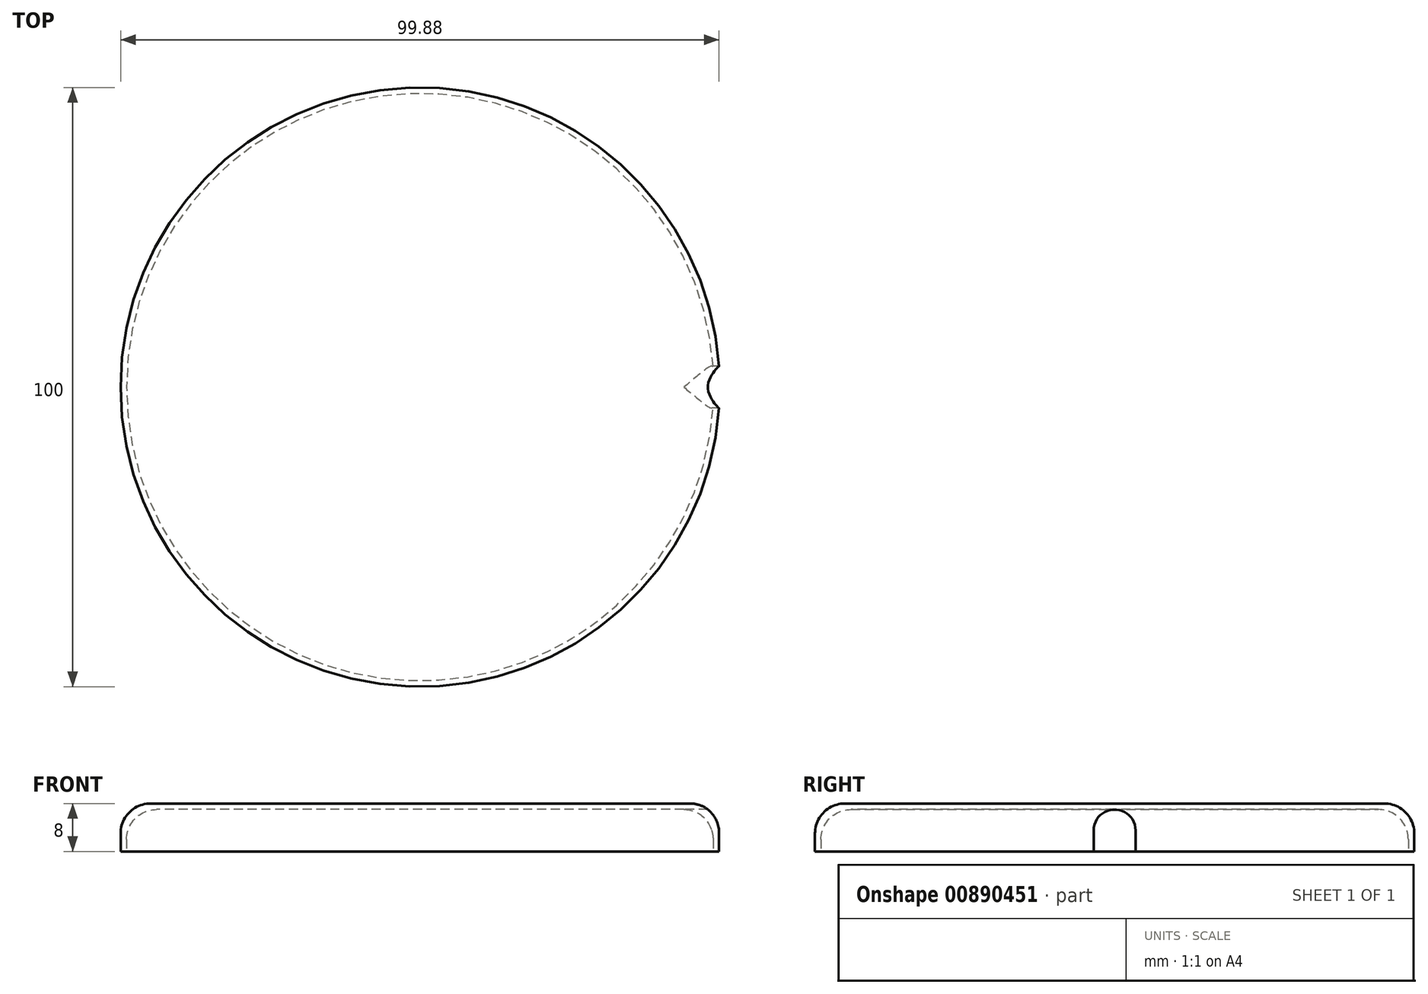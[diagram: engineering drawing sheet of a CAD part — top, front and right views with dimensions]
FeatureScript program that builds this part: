
annotation { "Feature Type Name" : "Feature", "Feature Type Description" : "" }
export const myFeature = defineFeature(function(context is Context, id is Id, definition is map)
    precondition{}
    {
        {
            var Q0;
            Q0=qCreatedBy(makeId("Front.planeOp"),FACE);
            var sketch = newSketch(context, id + "F0", { "sketchPlane" : qUnion([Q0])});
            skLineSegment(sketch, "E0", {"start": v(0, 0) * mm, "end": v(0, 8) * mm, "construction": true});
            skLineSegment(sketch, "E1", {"start": v(50, 0) * mm, "end": v(50, 3) * mm});
            skLineSegment(sketch, "E2", {"start": v(45, 8) * mm, "end": v(0, 8) * mm});
            skLineSegment(sketch, "E3", {"start": v(50, 0) * mm, "end": v(49, 0) * mm});
            skLineSegment(sketch, "E4", {"start": v(49, 0) * mm, "end": v(49, 2) * mm});
            skLineSegment(sketch, "E5", {"start": v(44, 7) * mm, "end": v(0, 7) * mm});
            skPoint(sketch, "E6.visualSharp", {"position": v(49, 7) * mm});
            skArc(sketch, "E6.filletArc", {"start": v(49, 2) * mm, "mid": v(47.54, 5.54) * mm, "end": v(44, 7) * mm});
            skPoint(sketch, "E7.visualSharp", {"position": v(50, 8) * mm});
            skArc(sketch, "E7.filletArc", {"start": v(50, 3) * mm, "mid": v(48.54, 6.54) * mm, "end": v(45, 8) * mm});
            skLineSegment(sketch, "E8", {"start": v(0, 7) * mm, "end": v(0, 8) * mm});
            skSolve(sketch);
        }
        {
            var Q0;
            Q0=makeQuery(id+"F0.imprint","IMPRINT",FACE,{"disambiguationData":[TD([[makeQuery(id+"F0.imprint","IMPRINT",EDGE,{"derivedFrom":sQuery(id+"F0.wireOp",EDGE,"E1")}),1.0]])]});
            var Q1;
            Q1=sQuery(id+"F0.wireOp",EDGE,"E0");
            revolve(context, id + "F1", {"surfaceOperationType" : NewSurfaceOperationType.NEW, "entities" : qUnion([Q0]), "axis" : qUnion([Q1]), "revolveType" : RevolveType.FULL});
        }
        {
            var Q0;
            Q0=makeQuery(id+"F1.opRevolve","SWEPT_FACE",FACE,{"disambiguationData":[OSD([sQuery(id+"F0.wireOp",EDGE,"E1")])]});
            cPlane(context, id + "F2", {"entities" : qUnion([Q0]), "cplaneType" : CPlaneType.LINE_ANGLE, "offset" : 25 * mm, "angle" : 0 * degree, "width" : 150 * mm, "height" : 150 * mm});
        }
        {
            var Q0;
            Q0=qCreatedBy(id+"F2.planeOp",FACE);
            var sketch = newSketch(context, id + "F3", { "sketchPlane" : qUnion([Q0])});
            skLineSegment(sketch, "E9", {"start": v(0, 0) * mm, "end": v(-3.5, 0) * mm});
            skLineSegment(sketch, "E10", {"start": v(-3.5, 0) * mm, "end": v(-3.5, 3.5) * mm});
            skLineSegment(sketch, "E11", {"start": v(3.5, 3.5) * mm, "end": v(3.5, 0) * mm});
            skLineSegment(sketch, "E12", {"start": v(3.5, 0) * mm, "end": v(0, 0) * mm});
            skLineSegment(sketch, "E13", {"start": v(0, 7) * mm, "end": v(0, 7) * mm});
            skPoint(sketch, "E14.visualSharp", {"position": v(-3.5, 7) * mm});
            skArc(sketch, "E14.filletArc", {"start": v(0, 7) * mm, "mid": v(-2.47, 5.97) * mm, "end": v(-3.5, 3.5) * mm});
            skPoint(sketch, "E15.visualSharp", {"position": v(3.5, 7) * mm});
            skArc(sketch, "E15.filletArc", {"start": v(3.5, 3.5) * mm, "mid": v(2.47, 5.97) * mm, "end": v(0, 7) * mm});
            skSolve(sketch);
        }
        {
            var Q0;
            Q0=makeQuery(id+"F3.imprint","IMPRINT",FACE,{"disambiguationData":[TD([[makeQuery(id+"F3.imprint","IMPRINT",EDGE,{"derivedFrom":sQuery(id+"F3.wireOp",EDGE,"E9")}),-1.0]])]});
            extrude(context, id + "F4", {"entities" : qUnion([Q0]), "operationType" : NewBodyOperationType.REMOVE, "oppositeDirection" : true, "depth" : 75 * mm, "offsetDistance" : 25 * mm});
        }
    });
